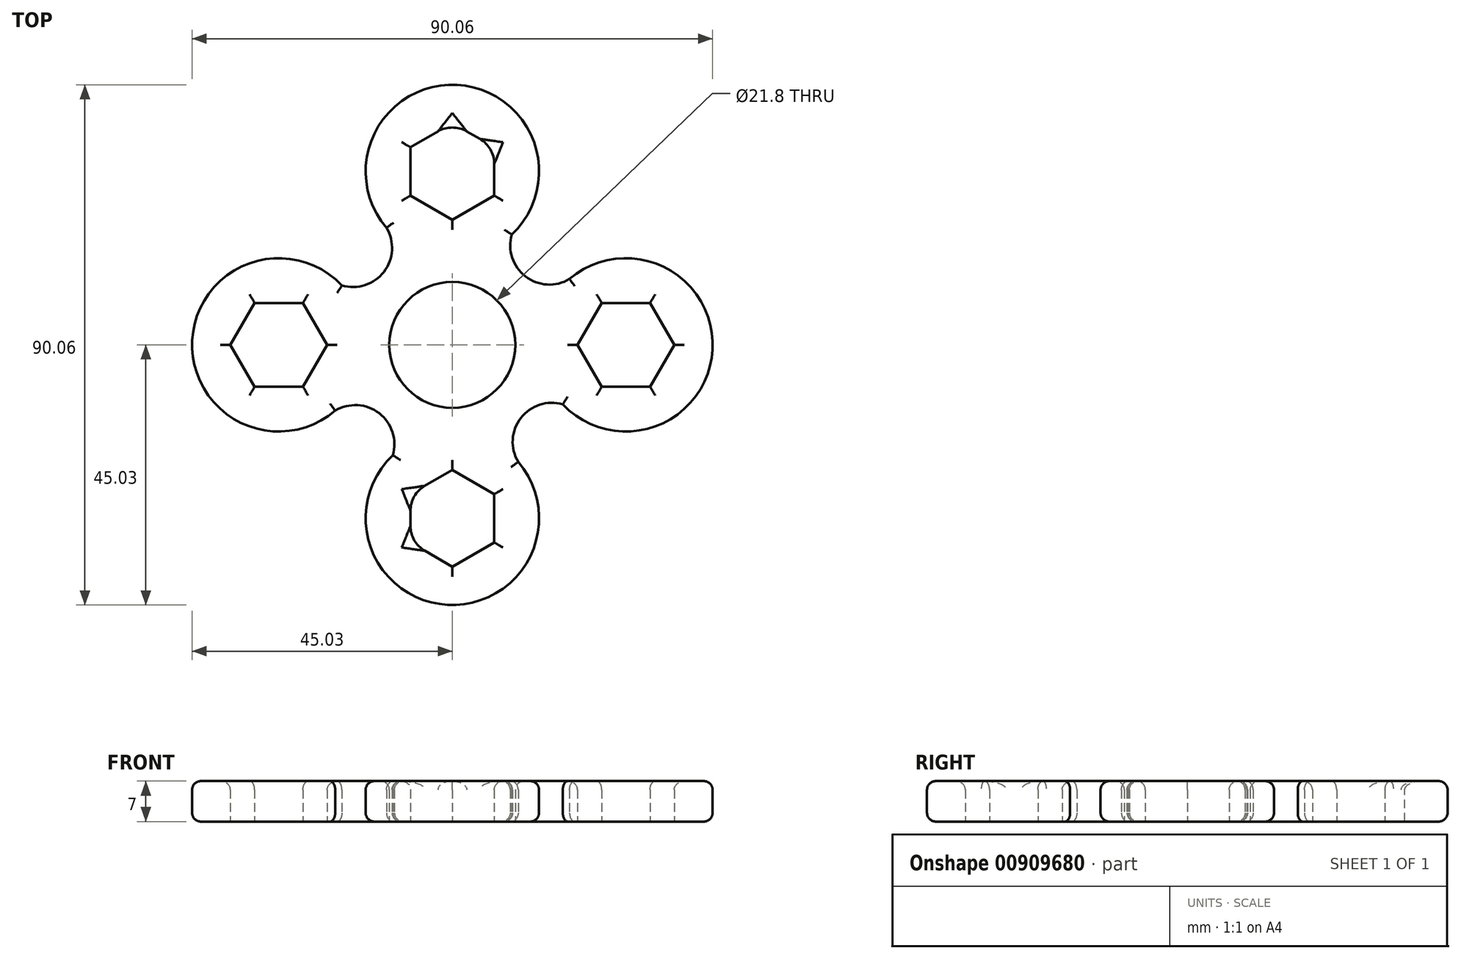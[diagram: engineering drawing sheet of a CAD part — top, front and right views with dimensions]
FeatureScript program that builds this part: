
annotation { "Feature Type Name" : "Feature", "Feature Type Description" : "" }
export const myFeature = defineFeature(function(context is Context, id is Id, definition is map)
    precondition{}
    {
        {
            var Q0;
            Q0=qCreatedBy(makeId("Top.planeOp"),FACE);
            var sketch = newSketch(context, id + "F0", { "sketchPlane" : qUnion([Q0])});
            skCircle(sketch, "E0", {"center": v(0, 0) * mm, "radius": 10.9 * mm});
            skLineSegment(sketch, "E1", {"start": v(-8.83, -9.81) * mm, "end": v(-8.83, -9.81) * mm});
            skCircle(sketch, "E2", {"center": v(0, 30.03) * mm, "radius": 15 * mm});
            skCircle(sketch, "E3.1.0", {"center": v(-30.03, 0) * mm, "radius": 15 * mm});
            skCircle(sketch, "E3.2.0", {"center": v(0, -30.03) * mm, "radius": 15 * mm});
            skCircle(sketch, "E3.3.0", {"center": v(30.03, 0) * mm, "radius": 15 * mm});
            skArc(sketch, "E4", {"start": v(10.29, 19.11) * mm, "mid": v(12.65, 11.84) * mm, "end": v(20.28, 11.4) * mm});
            skPoint(sketch, "E5.endSnap0", {"position": v(-11.84, -6.49) * mm});
            skArc(sketch, "E6.1.0", {"start": v(-19.11, 10.29) * mm, "mid": v(-11.84, 12.65) * mm, "end": v(-11.4, 20.28) * mm});
            skArc(sketch, "E6.2.0", {"start": v(-10.29, -19.11) * mm, "mid": v(-12.65, -11.84) * mm, "end": v(-20.28, -11.4) * mm});
            skArc(sketch, "E6.3.0", {"start": v(19.11, -10.29) * mm, "mid": v(11.84, -12.65) * mm, "end": v(11.4, -20.28) * mm});
            skCircle(sketch, "E7.cCircle", {"center": v(0, 30.03) * mm, "radius": 7.25 * mm, "construction": true});
            skLineSegment(sketch, "E7.0", {"start": v(7.25, 34.21) * mm, "end": v(7.25, 25.84) * mm});
            skLineSegment(sketch, "E7.1", {"start": v(7.25, 25.84) * mm, "end": v(0, 21.66) * mm});
            skLineSegment(sketch, "E7.2", {"start": v(0, 21.66) * mm, "end": v(-7.25, 25.84) * mm});
            skLineSegment(sketch, "E7.3", {"start": v(-7.25, 25.84) * mm, "end": v(-7.25, 34.21) * mm});
            skLineSegment(sketch, "E7.4", {"start": v(-7.25, 34.21) * mm, "end": v(0, 38.4) * mm});
            skLineSegment(sketch, "E7.5", {"start": v(0, 38.4) * mm, "end": v(7.25, 34.21) * mm});
            skPoint(sketch, "E7.0.midPoint", {"position": v(7.25, 30.03) * mm});
            skLineSegment(sketch, "E8.1.0", {"start": v(-25.84, 7.25) * mm, "end": v(-21.66, 0) * mm});
            skLineSegment(sketch, "E8.1.1", {"start": v(-34.21, 7.25) * mm, "end": v(-25.84, 7.25) * mm});
            skLineSegment(sketch, "E8.1.2", {"start": v(-38.4, 0) * mm, "end": v(-34.21, 7.25) * mm});
            skLineSegment(sketch, "E8.1.3", {"start": v(-34.21, -7.25) * mm, "end": v(-38.4, 0) * mm});
            skLineSegment(sketch, "E8.1.4", {"start": v(-25.84, -7.25) * mm, "end": v(-34.21, -7.25) * mm});
            skLineSegment(sketch, "E8.1.5", {"start": v(-21.66, 0) * mm, "end": v(-25.84, -7.25) * mm});
            skLineSegment(sketch, "E8.2.0", {"start": v(-7.25, -25.84) * mm, "end": v(0, -21.66) * mm});
            skLineSegment(sketch, "E8.2.1", {"start": v(-7.25, -34.21) * mm, "end": v(-7.25, -25.84) * mm});
            skLineSegment(sketch, "E8.2.2", {"start": v(0, -38.4) * mm, "end": v(-7.25, -34.21) * mm});
            skLineSegment(sketch, "E8.2.3", {"start": v(7.25, -34.21) * mm, "end": v(0, -38.4) * mm});
            skLineSegment(sketch, "E8.2.4", {"start": v(7.25, -25.84) * mm, "end": v(7.25, -34.21) * mm});
            skLineSegment(sketch, "E8.2.5", {"start": v(0, -21.66) * mm, "end": v(7.25, -25.84) * mm});
            skLineSegment(sketch, "E8.3.0", {"start": v(25.84, -7.25) * mm, "end": v(21.66, 0) * mm});
            skLineSegment(sketch, "E8.3.1", {"start": v(34.21, -7.25) * mm, "end": v(25.84, -7.25) * mm});
            skLineSegment(sketch, "E8.3.2", {"start": v(38.4, 0) * mm, "end": v(34.21, -7.25) * mm});
            skLineSegment(sketch, "E8.3.3", {"start": v(34.21, 7.25) * mm, "end": v(38.4, 0) * mm});
            skLineSegment(sketch, "E8.3.4", {"start": v(25.84, 7.25) * mm, "end": v(34.21, 7.25) * mm});
            skLineSegment(sketch, "E8.3.5", {"start": v(21.66, 0) * mm, "end": v(25.84, 7.25) * mm});
            skPoint(sketch, "E9.center", {"position": v(0, -0.03) * mm});
            skPoint(sketch, "E10.orphan", {"position": v(33.28, -19.24) * mm});
            skSolve(sketch);
        }
        {
            var Q0;
            Q0=makeQuery(id+"F0.imprint","IMPRINT",FACE,{"disambiguationData":[TD([[makeQuery(id+"F0.imprint","IMPRINT",EDGE,{"derivedFrom":sQuery(id+"F0.wireOp",EDGE,"E3.3.1")}),-1.0]])]});
            var Q1;
            Q1=makeQuery(id+"F0.imprint","IMPRINT",FACE,{"disambiguationData":[TD([[makeQuery(id+"F0.imprint","IMPRINT",EDGE,{"derivedFrom":sQuery(id+"F0.wireOp",EDGE,"E3.2.1")}),-1.0]])]});
            var Q2;
            Q2=makeQuery(id+"F0.imprint","IMPRINT",FACE,{"disambiguationData":[TD([[makeQuery(id+"F0.imprint","IMPRINT",EDGE,{"derivedFrom":sQuery(id+"F0.wireOp",EDGE,"JNXqZKiK-GkhN-0bhT-sdxq-lls9bOzlz7iW")}),-1.0]])]});
            var Q3;
            Q3=makeQuery(id+"F0.imprint","IMPRINT",FACE,{"disambiguationData":[TD([[makeQuery(id+"F0.imprint","IMPRINT",EDGE,{"derivedFrom":sQuery(id+"F0.wireOp",EDGE,"E3.1.1")}),-1.0]])]});
            var Q4;
            Q4=makeQuery(id+"F0.imprint","IMPRINT",FACE,{"disambiguationData":[TD([[makeQuery(id+"F0.imprint","IMPRINT",EDGE,{"derivedFrom":sQuery(id+"F0.wireOp",EDGE,"E8.1.0")}),1.0]])]});
            var Q5;
            Q5=makeQuery(id+"F0.imprint","IMPRINT",FACE,{"disambiguationData":[TD([[makeQuery(id+"F0.imprint","IMPRINT",EDGE,{"derivedFrom":sQuery(id+"F0.wireOp",EDGE,"E8.2.0")}),1.0]])]});
            var Q6;
            Q6=makeQuery(id+"F0.imprint","IMPRINT",FACE,{"disambiguationData":[TD([[makeQuery(id+"F0.imprint","IMPRINT",EDGE,{"derivedFrom":sQuery(id+"F0.wireOp",EDGE,"E0")}),-1.0]])]});
            var Q7;
            Q7=makeQuery(id+"F0.imprint","IMPRINT",FACE,{"disambiguationData":[TD([[makeQuery(id+"F0.imprint","IMPRINT",EDGE,{"derivedFrom":sQuery(id+"F0.wireOp",EDGE,"E8.3.0")}),1.0]])]});
            var Q8;
            Q8=makeQuery(id+"F0.imprint","IMPRINT",FACE,{"disambiguationData":[TD([[makeQuery(id+"F0.imprint","IMPRINT",EDGE,{"derivedFrom":sQuery(id+"F0.wireOp",EDGE,"E7.0")}),1.0]])]});
            var Q9;
            {var subQ0=sQuery(id+"F0.wireOp",EDGE,"E9.1.4");Q9=makeQuery(id+"F0.imprint","IMPRINT",FACE,{"disambiguationData":[TD([[makeQuery(id+"F0.imprint","IMPRINT",EDGE,{"derivedFrom":subQ0}),-1.0]])]});}
            extrude(context, id + "F1", {"entities" : qUnion([Q0, Q1, Q2, Q3, Q4, Q5, Q6, Q7, Q8, Q9]), "depth" : 7 * mm, "offsetDistance" : 25 * mm});
        }
        {
            var Q0;
            Q0=makeQuery(id+"F1.opExtrude","CAP_EDGE",EDGE,{"disambiguationData":[OSD([sQuery(id+"F0.wireOp",EDGE,"E3.3.0")])],"isStart":true});
            var Q1;
            Q1=makeQuery(id+"F1.opExtrude","CAP_EDGE",EDGE,{"disambiguationData":[OSD([sQuery(id+"F0.wireOp",EDGE,"E4")])],"isStart":true});
            var Q2;
            Q2=makeQuery(id+"F1.opExtrude","CAP_EDGE",EDGE,{"disambiguationData":[OSD([sQuery(id+"F0.wireOp",EDGE,"E2")])],"isStart":true});
            var Q3;
            Q3=makeQuery(id+"F1.opExtrude","CAP_EDGE",EDGE,{"disambiguationData":[OSD([sQuery(id+"F0.wireOp",EDGE,"E6.1.0")])],"isStart":true});
            var Q4;
            Q4=makeQuery(id+"F1.opExtrude","CAP_EDGE",EDGE,{"disambiguationData":[OSD([sQuery(id+"F0.wireOp",EDGE,"E3.1.0")])],"isStart":true});
            var Q5;
            Q5=makeQuery(id+"F1.opExtrude","CAP_EDGE",EDGE,{"disambiguationData":[OSD([sQuery(id+"F0.wireOp",EDGE,"E3.2.0")])],"isStart":true});
            var Q6;
            Q6=makeQuery(id+"F1.opExtrude","CAP_EDGE",EDGE,{"disambiguationData":[OSD([sQuery(id+"F0.wireOp",EDGE,"E6.2.0")])],"isStart":true});
            var Q7;
            Q7=makeQuery(id+"F1.opExtrude","CAP_EDGE",EDGE,{"disambiguationData":[OSD([sQuery(id+"F0.wireOp",EDGE,"E6.3.0")])],"isStart":true});
            var Q8;
            Q8=makeQuery(id+"F1.opExtrude","CAP_EDGE",EDGE,{"disambiguationData":[OSD([sQuery(id+"F0.wireOp",EDGE,"E3.2.0")])],"isStart":false});
            var Q9;
            Q9=makeQuery(id+"F1.opExtrude","CAP_EDGE",EDGE,{"disambiguationData":[OSD([sQuery(id+"F0.wireOp",EDGE,"E6.3.0")])],"isStart":false});
            var Q10;
            Q10=makeQuery(id+"F1.opExtrude","CAP_EDGE",EDGE,{"disambiguationData":[OSD([sQuery(id+"F0.wireOp",EDGE,"E3.3.0")])],"isStart":false});
            var Q11;
            Q11=makeQuery(id+"F1.opExtrude","CAP_FACE",FACE,{"disambiguationData":[OSD([sQuery(id+"F0.wireOp",EDGE,"E0"),sQuery(id+"F0.wireOp",EDGE,"E2"),sQuery(id+"F0.wireOp",EDGE,"E3.1.0"),sQuery(id+"F0.wireOp",EDGE,"E3.2.0"),sQuery(id+"F0.wireOp",EDGE,"E3.3.0"),sQuery(id+"F0.wireOp",EDGE,"E4"),sQuery(id+"F0.wireOp",EDGE,"E6.1.0"),sQuery(id+"F0.wireOp",EDGE,"E6.2.0"),sQuery(id+"F0.wireOp",EDGE,"E6.3.0"),sQuery(id+"F0.wireOp",EDGE,"E7.0"),sQuery(id+"F0.wireOp",EDGE,"E7.1"),sQuery(id+"F0.wireOp",EDGE,"E7.2"),sQuery(id+"F0.wireOp",EDGE,"E7.3"),sQuery(id+"F0.wireOp",EDGE,"E7.4"),sQuery(id+"F0.wireOp",EDGE,"E7.5"),sQuery(id+"F0.wireOp",EDGE,"E8.1.0"),sQuery(id+"F0.wireOp",EDGE,"E8.1.1"),sQuery(id+"F0.wireOp",EDGE,"E8.1.2"),sQuery(id+"F0.wireOp",EDGE,"E8.1.3"),sQuery(id+"F0.wireOp",EDGE,"E8.1.4"),sQuery(id+"F0.wireOp",EDGE,"E8.1.5"),sQuery(id+"F0.wireOp",EDGE,"E8.2.0"),sQuery(id+"F0.wireOp",EDGE,"E8.2.1"),sQuery(id+"F0.wireOp",EDGE,"E8.2.2"),sQuery(id+"F0.wireOp",EDGE,"E8.2.3"),sQuery(id+"F0.wireOp",EDGE,"E8.2.4"),sQuery(id+"F0.wireOp",EDGE,"E8.2.5"),sQuery(id+"F0.wireOp",EDGE,"E8.3.0"),sQuery(id+"F0.wireOp",EDGE,"E8.3.1"),sQuery(id+"F0.wireOp",EDGE,"E8.3.2"),sQuery(id+"F0.wireOp",EDGE,"E8.3.3"),sQuery(id+"F0.wireOp",EDGE,"E8.3.4"),sQuery(id+"F0.wireOp",EDGE,"E8.3.5")])],"isStart":false});
            var Q12;
            Q12=makeQuery(id+"F1.opExtrude","CAP_EDGE",EDGE,{"disambiguationData":[OSD([sQuery(id+"F0.wireOp",EDGE,"E2")])],"isStart":false});
            var Q13;
            Q13=makeQuery(id+"F1.opExtrude","CAP_EDGE",EDGE,{"disambiguationData":[OSD([sQuery(id+"F0.wireOp",EDGE,"E6.1.0")])],"isStart":false});
            var Q14;
            Q14=makeQuery(id+"F1.opExtrude","CAP_EDGE",EDGE,{"disambiguationData":[OSD([sQuery(id+"F0.wireOp",EDGE,"E3.1.0")])],"isStart":false});
            fillet(context, id + "F2", {"entities" : qUnion([Q0, Q1, Q2, Q3, Q4, Q5, Q6, Q7, Q8, Q9, Q10, Q11, Q12, Q13, Q14]), "radius" : 1.5 * mm, "tangentPropagation" : true, "allowEdgeOverflow" : false});
        }
        {
            var Q0;
            Q0=makeQuery(id+"F2.opFillet","BLEND_FACE",FACE,{"disambiguationData":[OSD([sQuery(id+"F0.wireOp",EDGE,"E8.2.1")])]});
            fillet(context, id + "F3", {"entities" : qUnion([Q0]), "radius" : 5 * mm, "tangentPropagation" : true, "allowEdgeOverflow" : false});
        }
        {
            var Q0;
            Q0=makeQuery(id+"F2.opFillet","BLEND_FACE",FACE,{"disambiguationData":[OSD([sQuery(id+"F0.wireOp",EDGE,"E7.5")])]});
            fillet(context, id + "F4", {"entities" : qUnion([Q0]), "radius" : 5 * mm, "tangentPropagation" : true, "allowEdgeOverflow" : false});
        }
    });
